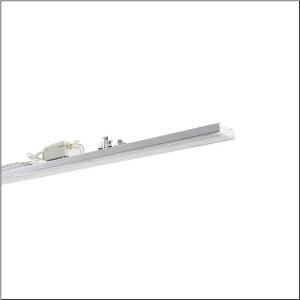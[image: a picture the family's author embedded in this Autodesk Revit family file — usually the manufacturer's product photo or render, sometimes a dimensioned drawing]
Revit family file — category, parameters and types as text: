
# Revit family: licross_21_recessed_mo_52te12dv4fxg3c
name_source: partatom
category: Lighting Fixtures
units: mm (PartAtom-declared; Revit-internal decimal feet)

## family parameters
Cut with Voids When Loaded = No
Host = Face
Light Source = No
Part Type = Normal
Room Calculation Point = No
Round Connector Dimension = Use Diameter
Shared = No

## types (1)
- --- (1 x LED, 950 lm, 5.5 W, 4000K)
    Apparent Load = 6 VA
    CIE Flux Codes = 72 92 99 100 100
    Color Rendering = 80
    Color Temperature = 4000K
    Default Elevation = 1800 mm
    Description = Licross 21 Recessed MO, luminaire insert, of sheet steel, galvanised, coil coated, white, length: 2.250mm, width: 66mm, height: 67mm, LED rated luminous flux: 15.420lm, light colour: 840, SDCM (Standard Deviation of Colour Matching)MacAdam ≤ 3 SDCM (initial), control gear: DALI 2 (for two DALI lines), with plug, 6-pole, with phase selection, for trunking rail, 14-core, mains connection: 220..240V, AC, 50/60Hz, rated input power: 89W, for trunking rail, 14-core, internal wiring halogen-free, for emergency light function, converter,control gear: single battery element, battery: LiFePO4, 9Ah, primary optical cover: cover, of PMMA, light emission: direct distribution, primary light characteristic: symmetric, protection rating (complete): IP54, insulation class (complete): insulation class I (protective earthing), certification: CE, UKCA, protection symbol: D if used in an environment with non-conductive dust loads with corresponding accessories, impact resistance: IK06, permissible ambient temperature for indoor applications: +5..+35°C, standard: EN 60598-2-22, LABS conformity tested according to VDMA 24364:2018-05, reducing of maximum allowable ambient temperature of 5°C with ceiling mounting, corresponds to IFS (International Featured Standards) requirements for safety and quality in the food industry, The light source and the operating device comply with the requirements of the Ecodesign Regulation (EU) 2019/2020 and are replaceable in accordance with this regulation, packaging unit: 1 piece
    Height = 58 mm
    Lamp = 1 x LED
    Lamp Light Flux = 950 lm
    Lamp Power = 5.5 W
    Lamp count = 1
    Length = 2250 mm
    Luminous efficacy = 173 lm/W
    Manufacturer = Siteco
    ModVariant = No
    Model = 52TE12DV4FXG3C
    Mounting Place = Ceiling
    Mounting Type = Pendant
    Number of Poles = 1
    OnlyDefault = Yes
    Power Factor = 1
    Product Name = Licross 21 Recessed MO
    Product group = luminaire insert | ceiling pendant
    ProductGroupID = 901
    Protection Class = Protection class I
    Protection Degree = IP 54
    RLX_Detail_Level = 1
    RLX_Emergency_Light_Flux = 0 lm
    RLX_Emergency_Type = 0
    RLX_Emergency_Type_DB = No
    RlxData = <blob elided: 30385 chars, md5=d1259fe8>
    Socket = socket
    Standby Power = 0 W
    System Light Flux = 950 lm
    System Power = 6 W
    Type Comments = : emergency light operation: 3 h
    Type Image = l_1296930.jpg
    URL = http://relux.com
    VarID = @adj_111569
    Voltage = 0 V
    Weight = 0.00 kg
    Width = 66 mm

## geometry (parser evidence)
native form markers: Blend x4, Sweep x10
no freeform markers — native parametric forms only
